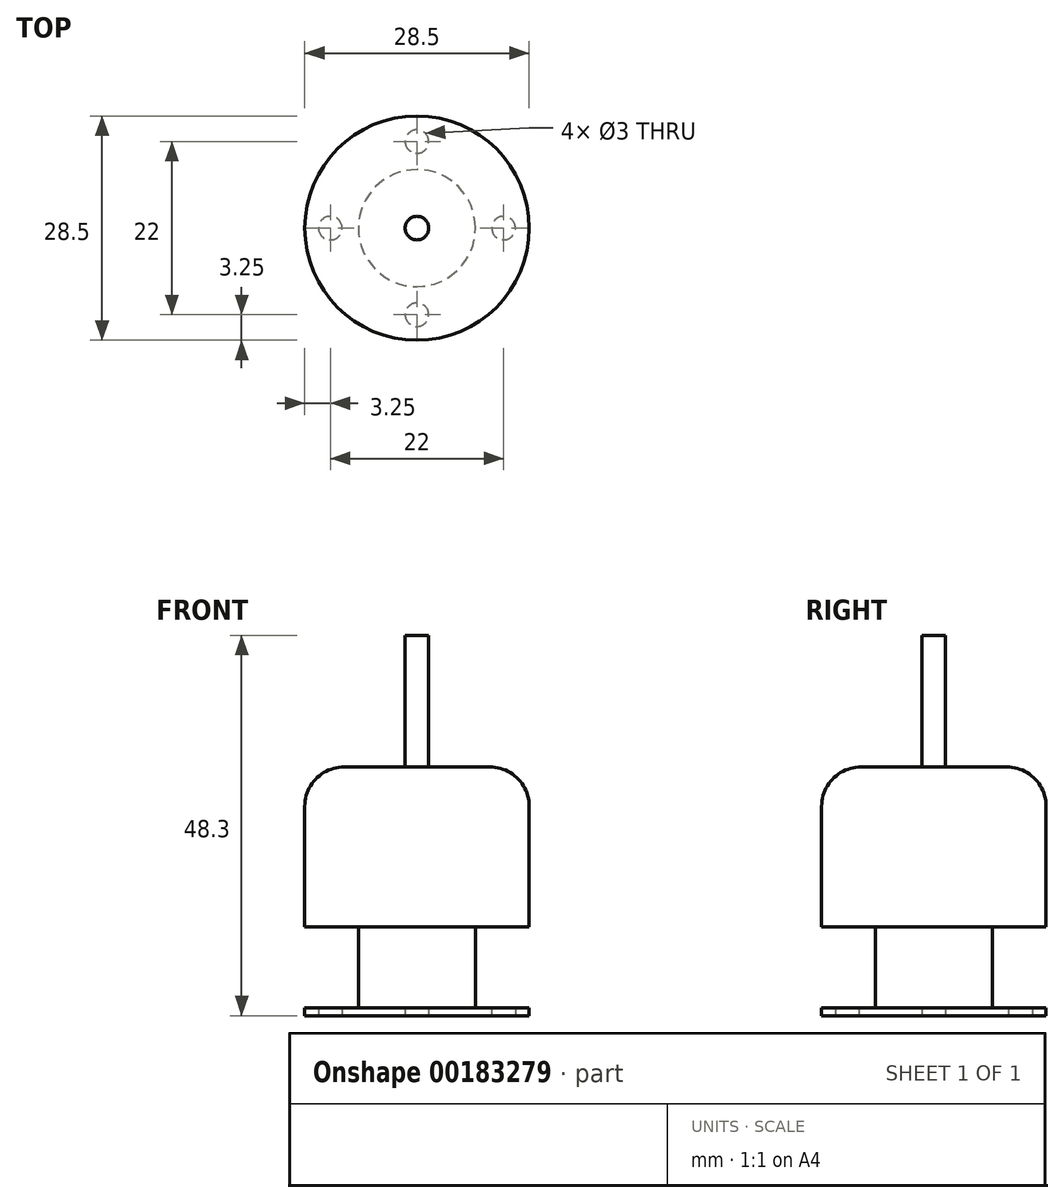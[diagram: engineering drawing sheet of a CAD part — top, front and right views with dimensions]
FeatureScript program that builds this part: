
annotation { "Feature Type Name" : "Feature", "Feature Type Description" : "" }
export const myFeature = defineFeature(function(context is Context, id is Id, definition is map)
    precondition{}
    {
        {
            var Q0;
            Q0=qCreatedBy(makeId("Top.planeOp"),FACE);
            var sketch = newSketch(context, id + "F0", { "sketchPlane" : qUnion([Q0])});
            skCircle(sketch, "E0", {"center": v(0, 0) * mm, "radius": 14.25 * mm});
            skSolve(sketch);
        }
        {
            var Q0;
            Q0 = qSketchRegion(id + "F0", true);
            extrude(context, id + "F1", {"entities" : qUnion([Q0]), "depth" : 1 * mm});
        }
        {
            var Q0;
            Q0=makeQuery(id+"F1.opExtrude","CAP_FACE",FACE,{"disambiguationData":[OSD([sQuery(id+"F0.wireOp",EDGE,"E0")])],"isStart":false});
            var sketch = newSketch(context, id + "F2", { "sketchPlane" : qUnion([Q0])});
            skCircle(sketch, "E1", {"center": v(0, 0) * mm, "radius": 7.43 * mm});
            skSolve(sketch);
        }
        {
            var Q0;
            Q0 = qSketchRegion(id + "F2", true);
            extrude(context, id + "F3", {"entities" : qUnion([Q0]), "operationType" : NewBodyOperationType.ADD, "depth" : 10.3 * mm});
        }
        {
            var Q0;
            Q0=makeQuery(id+"F3.opExtrude","CAP_FACE",FACE,{"disambiguationData":[OSD([sQuery(id+"F2.wireOp",EDGE,"E1")])],"isStart":false});
            var sketch = newSketch(context, id + "F4", { "sketchPlane" : qUnion([Q0])});
            skCircle(sketch, "E2.0", {"center": v(0, 0) * mm, "radius": 14.25 * mm});
            skSolve(sketch);
        }
        {
            var Q0;
            Q0 = qSketchRegion(id + "F4", true);
            extrude(context, id + "F5", {"entities" : qUnion([Q0]), "operationType" : NewBodyOperationType.ADD, "depth" : 20.3 * mm});
        }
        {
            var Q0;
            Q0=makeQuery(id+"F5.opExtrude","CAP_EDGE",EDGE,{"disambiguationData":[OSD([sQuery(id+"F4.wireOp",EDGE,"E2.0")])],"isStart":false});
            fillet(context, id + "F6", {"entities" : qUnion([Q0]), "radius" : 5 * mm, "tangentPropagation" : true, "allowEdgeOverflow" : false});
        }
        {
            var Q0;
            Q0=makeQuery(id+"F5.opExtrude","CAP_FACE",FACE,{"disambiguationData":[OSD([sQuery(id+"F4.wireOp",EDGE,"E2.0")])],"isStart":false});
            var sketch = newSketch(context, id + "F7", { "sketchPlane" : qUnion([Q0])});
            skCircle(sketch, "E3", {"center": v(0, 0) * mm, "radius": 1.5 * mm});
            skSolve(sketch);
        }
        {
            var Q0;
            Q0 = qSketchRegion(id + "F7", true);
            extrude(context, id + "F8", {"entities" : qUnion([Q0]), "operationType" : NewBodyOperationType.ADD, "depth" : 16.7 * mm});
        }
        {
            var Q0;
            Q0=makeQuery(id+"F1.opExtrude","CAP_FACE",FACE,{"disambiguationData":[OSD([sQuery(id+"F0.wireOp",EDGE,"E0")])],"isStart":true});
            var sketch = newSketch(context, id + "F9", { "sketchPlane" : qUnion([Q0])});
            skCircle(sketch, "E4", {"center": v(0, 0) * mm, "radius": 11 * mm, "construction": true});
            skCircle(sketch, "E5", {"center": v(0, 11) * mm, "radius": 1.5 * mm});
            skCircle(sketch, "E6", {"center": v(11, 0) * mm, "radius": 1.5 * mm});
            skCircle(sketch, "E7", {"center": v(-11, 0) * mm, "radius": 1.5 * mm});
            skCircle(sketch, "E8", {"center": v(0, -11) * mm, "radius": 1.5 * mm});
            skSolve(sketch);
        }
        {
            var Q0;
            Q0 = qSketchRegion(id + "F9", true);
            extrude(context, id + "F10", {"entities" : qUnion([Q0]), "operationType" : NewBodyOperationType.REMOVE, "endBound" : BoundingType.UP_TO_NEXT, "oppositeDirection" : true, "depth" : 25 * mm});
        }
    });
